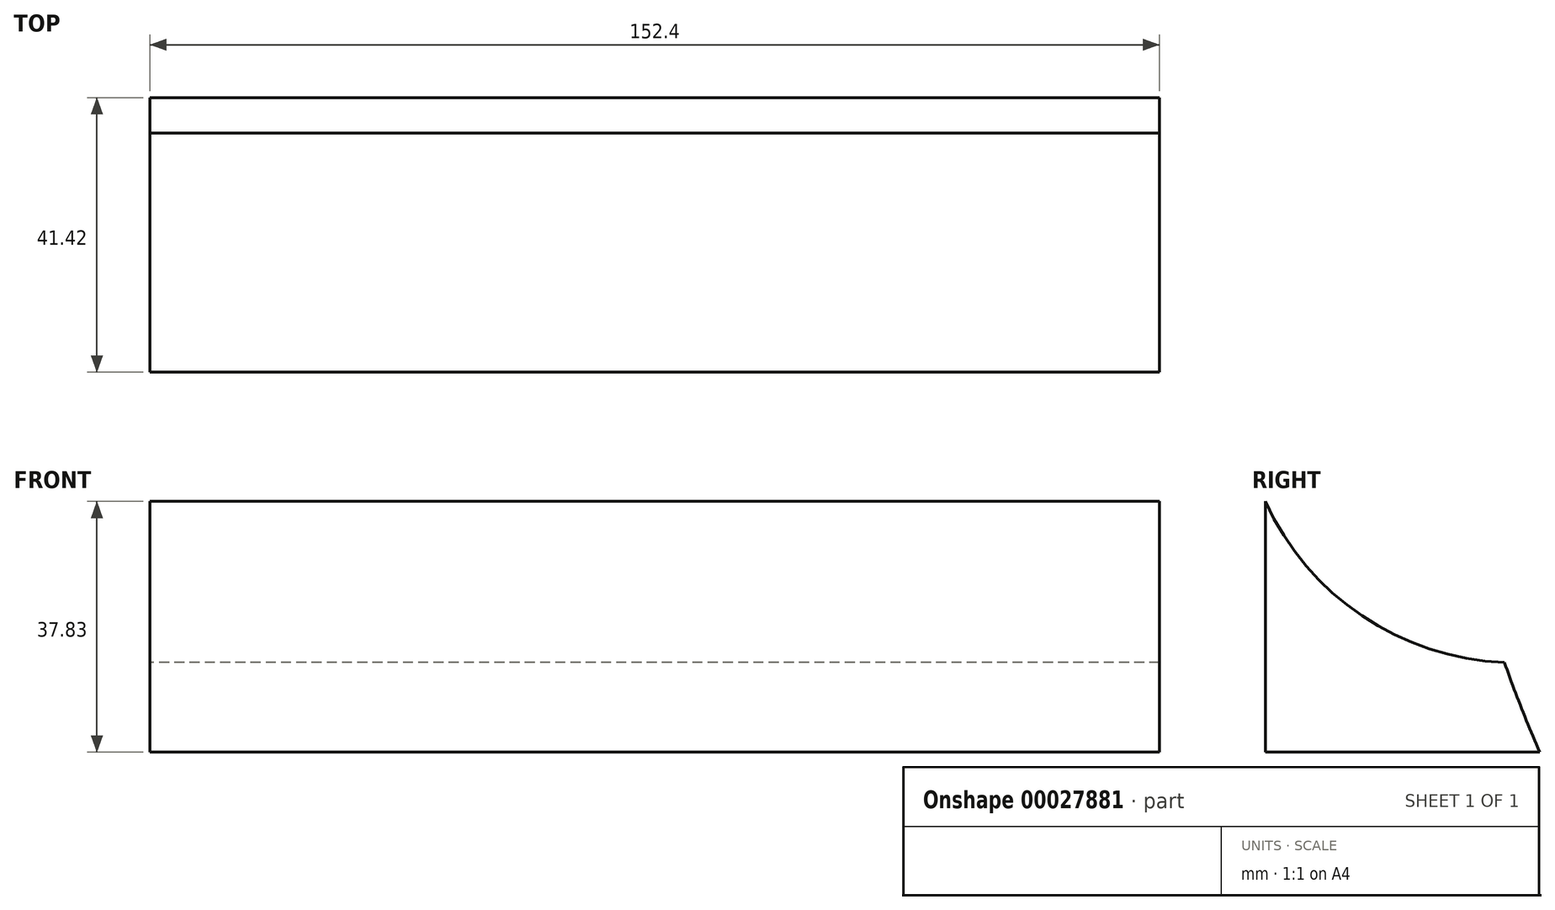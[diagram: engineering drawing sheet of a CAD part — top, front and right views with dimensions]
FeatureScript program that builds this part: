
annotation { "Feature Type Name" : "Feature", "Feature Type Description" : "" }
export const myFeature = defineFeature(function(context is Context, id is Id, definition is map)
    precondition{}
    {
        {
            var Q0;
            Q0=qCreatedBy(makeId("Right.planeOp"),FACE);
            var sketch = newSketch(context, id + "F0", { "sketchPlane" : qUnion([Q0])});
            skLineSegment(sketch, "E0.bottom", {"start": v(0, -3.5) * mm, "end": v(-120.56, -3.5) * mm});
            skLineSegment(sketch, "E0.top", {"start": v(0, 84.6) * mm, "end": v(-120.56, 84.6) * mm});
            skLineSegment(sketch, "E0.left", {"start": v(0, -3.5) * mm, "end": v(0, 84.6) * mm});
            skLineSegment(sketch, "E0.right", {"start": v(-120.56, -3.5) * mm, "end": v(-120.56, 84.6) * mm});
            skCircle(sketch, "E1", {"center": v(-82.85, 51.38) * mm, "radius": 41.4 * mm});
            skLineSegment(sketch, "E2", {"start": v(-82.85, 51.38) * mm, "end": v(49.8, 51.38) * mm});
            skLineSegment(sketch, "E3", {"start": v(49.8, 51.38) * mm, "end": v(44.56, -8.18) * mm});
            skFitSpline(sketch, "E4", {"points": [v(44.56, -8.18) * mm, v(-82.85, 51.38) * mm, v(-48.07, -59.93) * mm, v(-4.94, -90.68) * mm, v(44.56, -8.18) * mm]});
            skSolve(sketch);
        }
        {
            var Q0;
            Q0=makeQuery(id+"F0.imprint","IMPRINT",FACE,{"disambiguationData":[TD([[makeQuery(id+"F0.imprint","IMPRINT",EDGE,{"derivedFrom":sQuery(id+"F0.wireOp",EDGE,"E0.bottom")}),-1.0]])]});
            extrude(context, id + "F1", {"entities" : qUnion([Q0]), "depth" : 152.4 * mm});
        }
    });
